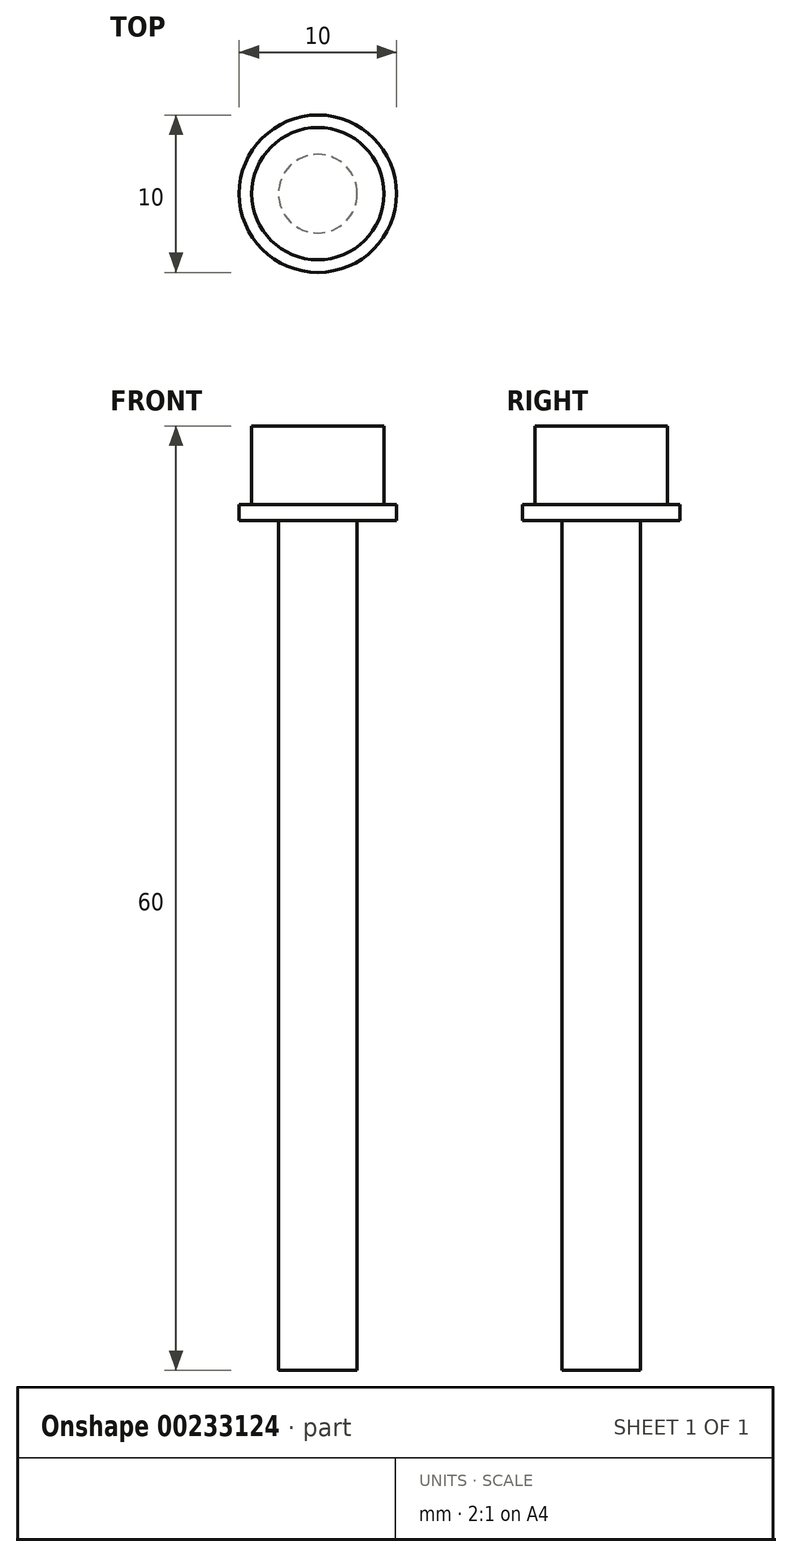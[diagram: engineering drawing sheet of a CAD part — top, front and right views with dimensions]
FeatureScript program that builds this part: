
annotation { "Feature Type Name" : "Feature", "Feature Type Description" : "" }
export const myFeature = defineFeature(function(context is Context, id is Id, definition is map)
    precondition{}
    {
        {
            var Q0;
            Q0=qCreatedBy(makeId("Top.planeOp"),FACE);
            var sketch = newSketch(context, id + "F0", { "sketchPlane" : qUnion([Q0])});
            skCircle(sketch, "E0", {"center": v(0, 0) * mm, "radius": 2.5 * mm});
            skSolve(sketch);
        }
        {
            var Q0;
            Q0=qSketchRegion(id+"F0",true);
            extrude(context, id + "F1", {"entities" : qUnion([Q0]), "oppositeDirection" : true, "depth" : 55 * mm});
        }
        {
            var Q0;
            Q0=qCreatedBy(makeId("Top.planeOp"),FACE);
            var sketch = newSketch(context, id + "F2", { "sketchPlane" : qUnion([Q0])});
            skCircle(sketch, "E1", {"center": v(0, 0) * mm, "radius": 4.2 * mm});
            skSolve(sketch);
        }
        {
            var Q0;
            Q0=qSketchRegion(id+"F2",true);
            extrude(context, id + "F3", {"entities" : qUnion([Q0]), "operationType" : NewBodyOperationType.ADD, "depth" : 5 * mm});
        }
        {
            var Q0;
            Q0=qCreatedBy(makeId("Top.planeOp"),FACE);
            var sketch = newSketch(context, id + "F4", { "sketchPlane" : qUnion([Q0])});
            skCircle(sketch, "E2", {"center": v(0, 0) * mm, "radius": 5 * mm});
            skSolve(sketch);
        }
        {
            var Q0;
            Q0=qSketchRegion(id+"F4",true);
            extrude(context, id + "F5", {"entities" : qUnion([Q0]), "operationType" : NewBodyOperationType.ADD, "oppositeDirection" : true, "depth" : 1 * mm});
        }
    });
